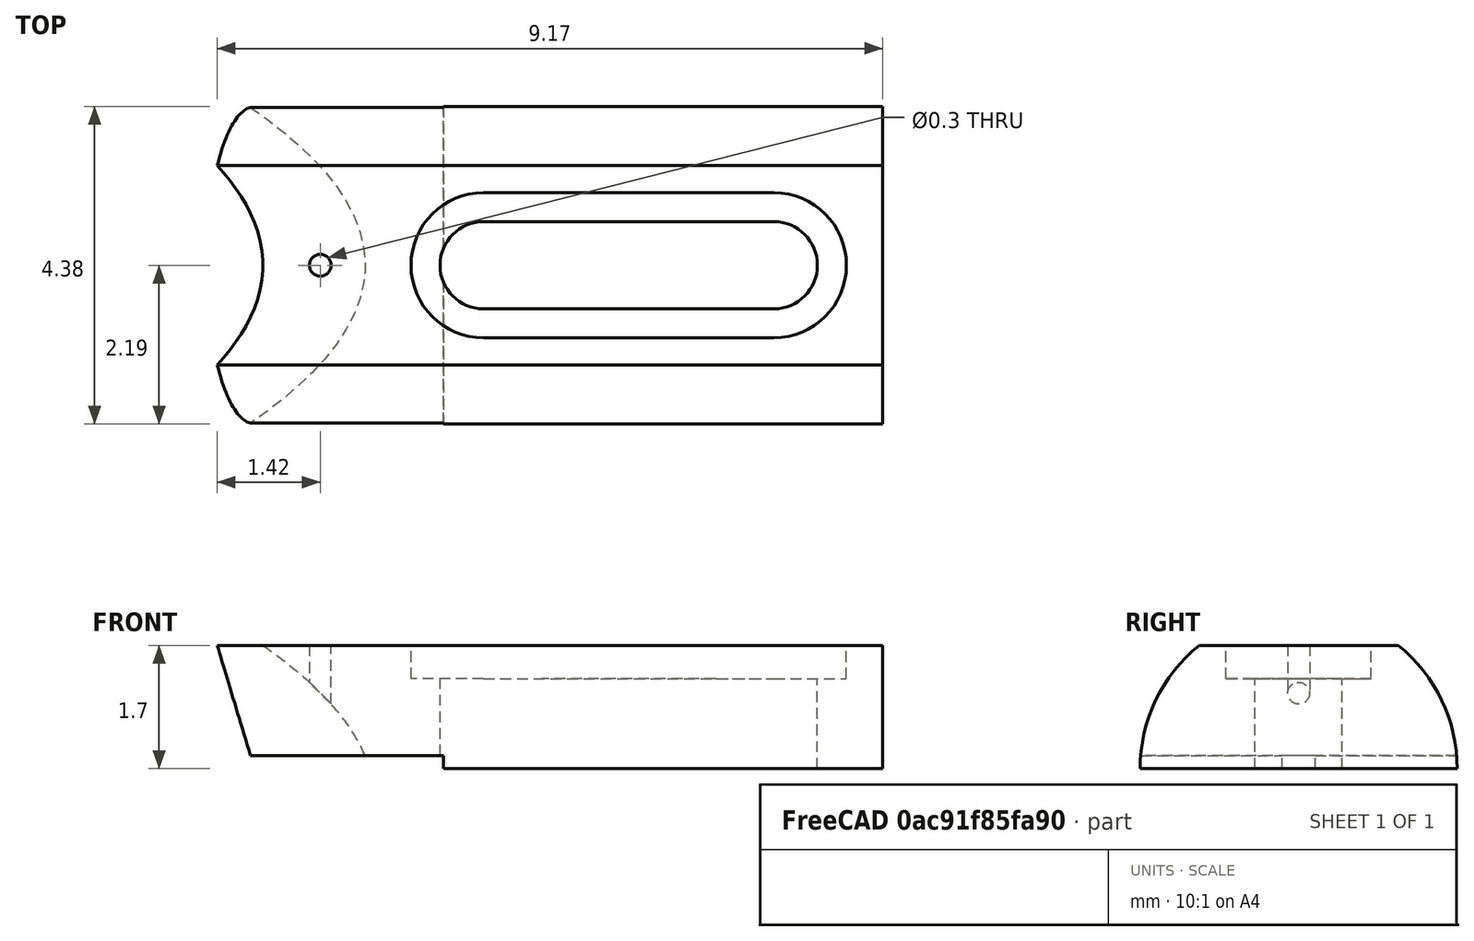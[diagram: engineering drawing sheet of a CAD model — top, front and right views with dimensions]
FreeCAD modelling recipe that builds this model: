
FCSTD DOCUMENT  (FreeCAD 0.19R24267 +99 (Git))
Label: parabolic_screwmount
License: All rights reserved
LicenseURL: http://en.wikipedia.org/wiki/All_rights_reserved
objects: Part::Cylinder×4, Part::Box×2, App::Link×1, Spreadsheet::Sheet×1, Part::Compound×1, Part::MultiFuse×1, Part::Cut×1
note: 9 computed .brp shape members not serialized (recipe doc carries the construction recipe); baked Part::Feature solids carry a one-line shape summary decoded from their .brp
EXTERNAL_REF file=parabolic_base.FCStd obj=Common
EXTERNAL_REF file=parabolic_base.FCStd obj=Spreadsheet

FEATURE [App::Link] Link  label="MirrorWithoutMount_Solid"
  LinkedObject = -> <external parabolic_base.FCStd>#Common
FEATURE [Spreadsheet::Sheet] Spreadsheet  label="ScrewMountParameters"
  cells = A1=Settings; E1=Importet properties (don't change here!); A2=Screw type; B2=M1; C2=Informative only (not updating below values); E2=Body offset; F2(body_offset)==<<parabolic_base>>#<<MirrorParameters>>.center_offset + <<parabolic_base>>#<<MirrorParameters>>.focal_length; G2=From parabolic_base: Offset of the body part with relation to Origin at the beamhole; A3=Through hole diameter; B3(mountscrew_through_dia)=1.2; C3=Close or medium fit diameter; E3=Body length; F3(body_length)==<<parabolic_base>>#<<MirrorParameters>>.tot_length; G3=From parabolic_base: Length of the body part; A4=Minimum material thickness; B4(min_material_thickness)=0.5; C4=Leave at least this amount of material if possible; E4=Body diameter; F4(body_width)==<<parabolic_base>>#<<MirrorParameters>>.max_width; G4=From parabolic_base: Diameter of body (max. width); A5=Screw head diameter; B5(screwhead_dia)=2; C5=Diameter of screw head; E5=Body height; F5(body_height)==<<parabolic_base>>#<<MirrorParameters>>.max_height; G5=From parabolic_base: Height of body (max body); A6=Screw head height max; B6(screwhead_height_max)==sqrt((body_width / 2) ^ 2 - (screwhead_dia / 2) ^ 2) - min_material_thickness; C6=Absolute maximum that leaves minimum material intact; A7=Screw head height real; B7(screwhead_height)=0.7; C7=Height of screw head; A8=Remaining material below screw head; B8(calculated_remaining_below_screwhead)==sqrt((body_width / 2) ^ 2 - (screwhead_dia / 2) ^ 2) - screwhead_height; C8=Remaining material below head of screw; A9=Remaining material on side of screw head; B9==(body_width - screwhead_dia) / 2; C9=Remaining material on both sides of the screw head; A10=Remaining material on side of screw; B10==(body_width - mountscrew_through_dia) / 2; C10=Remaining material on both sides of the screw
FEATURE [Part::Box] Box  label="CuttingToolThroughHole"
  AttacherType = Attacher::AttachEngine3D
  Height = 1.7
  Length = 4
  Placement = pos=(2.25,-0.6,0) rot=(0,0,1;0rad)
  Width = 1.2
  expr: Width = <<ScrewMountParameters>>.mountscrew_through_dia
  expr: Length = <<ScrewMountParameters>>.body_length - 2 * <<ScrewMountParameters>>.min_material_thickness - <<ScrewMountParameters>>.screwhead_dia
  expr: Height = <<ScrewMountParameters>>.body_height
  expr: .Placement.Base.y = -<<ScrewMountParameters>>.mountscrew_through_dia / 2
  expr: .Placement.Base.x = <<ScrewMountParameters>>.body_offset + <<ScrewMountParameters>>.min_material_thickness + <<ScrewMountParameters>>.screwhead_dia / 2
FEATURE [Part::Box] Box001  label="CuttingToolScrewHead"
  AttacherType = Attacher::AttachEngine3D
  Height = 0.942264
  Length = 4
  Placement = pos=(2.25,-1,1.24274) rot=(0,0,1;0rad)
  Width = 2
  expr: Width = <<ScrewMountParameters>>.screwhead_dia
  expr: Length = <<ScrewMountParameters>>.body_length - 2 * <<ScrewMountParameters>>.min_material_thickness - <<ScrewMountParameters>>.screwhead_dia
  expr: Height = <<ScrewMountParameters>>.body_width / 2 - <<ScrewMountParameters>>.calculated_remaining_below_screwhead
  expr: .Placement.Base.z = <<ScrewMountParameters>>.calculated_remaining_below_screwhead
  expr: .Placement.Base.y = -<<ScrewMountParameters>>.screwhead_dia / 2
  expr: .Placement.Base.x = <<ScrewMountParameters>>.body_offset + <<ScrewMountParameters>>.min_material_thickness + <<ScrewMountParameters>>.screwhead_dia / 2
FEATURE [Part::Compound] Compound
  Links = -> [Link]
FEATURE [Part::Cylinder] Cylinder  label="HeadFront"
  Angle = 360
  AttacherType = Attacher::AttachEngine3D
  Height = 10
  Placement = pos=(2.25,0,1.24274) rot=(0,0,1;0rad)
  Radius = 1
  expr: .Placement.Base.x = <<ScrewMountParameters>>.body_offset + <<ScrewMountParameters>>.min_material_thickness + <<ScrewMountParameters>>.screwhead_dia / 2
  expr: .Placement.Base.z = <<ScrewMountParameters>>.calculated_remaining_below_screwhead
  expr: Radius = <<ScrewMountParameters>>.screwhead_dia / 2
FEATURE [Part::Cylinder] Cylinder001  label="HeadBack"
  Angle = 360
  AttacherType = Attacher::AttachEngine3D
  Height = 10
  Placement = pos=(6.25,0,1.24274) rot=(0,0,1;0rad)
  Radius = 1
  expr: Radius = <<ScrewMountParameters>>.screwhead_dia / 2
  expr: .Placement.Base.z = <<ScrewMountParameters>>.calculated_remaining_below_screwhead
  expr: .Placement.Base.x = <<ScrewMountParameters>>.body_offset + <<ScrewMountParameters>>.min_material_thickness + <<ScrewMountParameters>>.screwhead_dia / 2 + <<ScrewMountParameters>>.body_length - 2 * <<ScrewMountParameters>>.min_material_thickness - <<ScrewMountParameters>>.screwhead_dia
FEATURE [Part::Cylinder] Cylinder002  label="ScrewThroughFront"
  Angle = 360
  AttacherType = Attacher::AttachEngine3D
  Height = 10
  Placement = pos=(2.25,0,0) rot=(0,0,1;0rad)
  Radius = 0.6
  expr: .Placement.Base.y = 0
  expr: Radius = <<ScrewMountParameters>>.mountscrew_through_dia / 2
  expr: .Placement.Base.x = <<ScrewMountParameters>>.body_offset + <<ScrewMountParameters>>.min_material_thickness + <<ScrewMountParameters>>.screwhead_dia / 2
FEATURE [Part::Cylinder] Cylinder003  label="ScrewThroughBack"
  Angle = 360
  AttacherType = Attacher::AttachEngine3D
  Height = 10
  Placement = pos=(6.25,0,0) rot=(0,0,1;0rad)
  Radius = 0.6
  expr: .Placement.Base.x = <<ScrewMountParameters>>.body_offset + <<ScrewMountParameters>>.min_material_thickness + <<ScrewMountParameters>>.screwhead_dia / 2 + <<ScrewMountParameters>>.body_length - 2 * <<ScrewMountParameters>>.min_material_thickness - <<ScrewMountParameters>>.screwhead_dia
  expr: Radius = <<ScrewMountParameters>>.mountscrew_through_dia / 2
FEATURE [Part::MultiFuse] Fusion  label="CuttingTools"
  Shapes = -> [Box001,Box,Cylinder,Cylinder001,Cylinder002,Cylinder003]
FEATURE [Part::Cut] Cut  label="ParabolicMirrorWithScrewmount"
  Base = -> Compound
  Tool = -> Fusion
